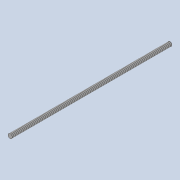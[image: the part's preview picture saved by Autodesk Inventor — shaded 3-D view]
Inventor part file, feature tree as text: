
AUTODESK INVENTOR PART (.ipt)
format: ipt  version: 2020 (Build 240168000, 168)  size: 107,520 bytes
history: native  units: mm
features: extrude x1, thread x1, sketch x1
ambient origin geometry x8: Origin, YZ Plane, XZ Plane, XY Plane, X Axis, Y Axis, Z Axis, Center Point
bodies: Solid1 (feature_tree)
feature tree (3):
  extrude  "Extrusion1"  Depth=150.0mm TaperAngle=0.0deg
  thread  "Thread1"  [1 undecoded]
  sketch  "Sketch1"  dims[d0=4.0mm d1=150.0mm d2=0.0mm d3=550.0mm d4=0.0mm]
note: 1 required parameter value undecoded (feature->parameter linkage not recoverable at this tier; creation-order binding heuristic only, values carry confidence <= 0.55)
